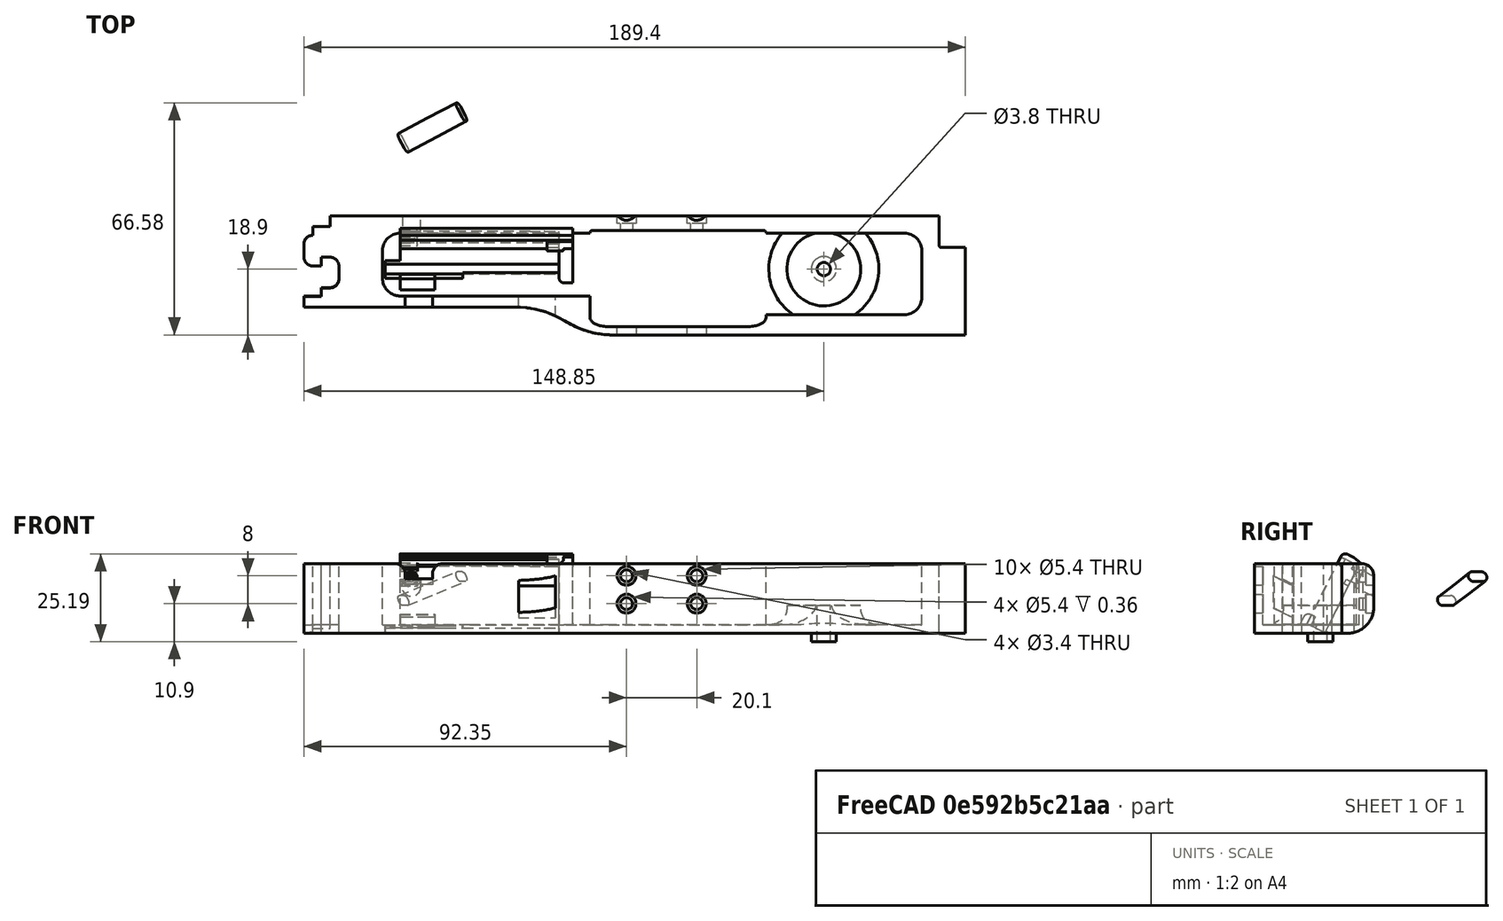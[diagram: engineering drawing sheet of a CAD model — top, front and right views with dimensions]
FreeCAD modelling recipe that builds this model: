
FCSTD DOCUMENT  (FreeCAD 0.19R0.19.2)
Label: v0_995
License: All rights reserved
LicenseURL: http://en.wikipedia.org/wiki/All_rights_reserved
objects: Sketcher::SketchObject×37, Part::Extrusion×31, Part::MultiFuse×19, Part::Box×14, Part::Cut×14, Part::Fillet×13, App::MeasureDistance×4, Part::Cylinder×4, Part::Revolution×1, Mesh::Feature×1
note: 133 computed .brp shape members not serialized (recipe doc carries the construction recipe); baked Part::Feature solids carry a one-line shape summary decoded from their .brp

FEATURE [Sketcher::SketchObject] Sketch
  FullyConstrained = true
  sketch-geometry (36):
    g0: LineSegment StartX=0 StartY=0 StartZ=0 EndX=154.4 EndY=0 EndZ=0
    g1: LineSegment StartX=154.4 StartY=0 StartZ=0 EndX=154.4 EndY=-7.6 EndZ=0
    g2: LineSegment StartX=32.5209 StartY=-26.2 StartZ=0 EndX=-7.5 EndY=-26.2 EndZ=0
    g3-g7: Circle x5 (B-spline internal-alignment scaffolding for g8; pole/knot coordinates omitted)
    g8: BSplineCurve PolesCount=5 KnotsCount=3 Degree=3 IsPeriodic=0
    g9: GeomPoint X=61.85 Y=-33.8 Z=0
    g10: GeomPoint X=47.185 Y=-29.9 Z=0
    g11: GeomPoint X=32.5209 Y=-26.2 Z=0
    g12: Circle CenterX=121.35 CenterY=-14.3 CenterZ=0 NormalX=0 NormalY=0 NormalZ=1 AngleXU=0 Radius=3.25
    g13: LineSegment StartX=-7.5 StartY=-26.2 StartZ=0 EndX=-27.5 EndY=-26.2 EndZ=0
    g14: LineSegment StartX=-20 StartY=0 StartZ=0 EndX=0 EndY=0 EndZ=0
    g15: LineSegment StartX=-25 StartY=-3.1 StartZ=0 EndX=-20 EndY=-3.1 EndZ=0
    g16: LineSegment StartX=-25 StartY=-3.1 StartZ=0 EndX=-25 EndY=-5.6 EndZ=0
    g17: LineSegment StartX=-27.5 StartY=-8.1 StartZ=0 EndX=-27.5 EndY=-11.85 EndZ=0
    g18: ArcOfCircle CenterX=-25 CenterY=-8.1 CenterZ=0 NormalX=0 NormalY=0 NormalZ=1 AngleXU=0 Radius=2.5 StartAngle=1.5708 EndAngle=3.14159
    g19: LineSegment StartX=-25 StartY=-14.35 StartZ=0 EndX=-22.5 EndY=-14.35 EndZ=0
    g20: ArcOfCircle CenterX=-25 CenterY=-11.85 CenterZ=0 NormalX=0 NormalY=0 NormalZ=1 AngleXU=0 Radius=2.5 StartAngle=3.14159 EndAngle=4.71239
    g21: LineSegment StartX=-22.5 StartY=-14.35 StartZ=0 EndX=-22.5 EndY=-11.85 EndZ=0
    g22: LineSegment StartX=-22.5 StartY=-11.85 StartZ=0 EndX=-20 EndY=-11.85 EndZ=0
    g23: ArcOfCircle CenterX=-20 CenterY=-14.35 CenterZ=0 NormalX=0 NormalY=0 NormalZ=1 AngleXU=0 Radius=2.5 StartAngle=8e-16 EndAngle=1.5708
    g24: LineSegment StartX=-17.5 StartY=-14.35 StartZ=0 EndX=-17.5 EndY=-18.1 EndZ=0
    g25: ArcOfCircle CenterX=-20 CenterY=-18.1 CenterZ=0 NormalX=0 NormalY=0 NormalZ=1 AngleXU=0 Radius=2.5 StartAngle=4.71239 EndAngle=6.28319
    g26: LineSegment StartX=-22.5 StartY=-20.6 StartZ=0 EndX=-20 EndY=-20.6 EndZ=0
    g27: LineSegment StartX=-22.5 StartY=-20.6 StartZ=0 EndX=-22.5 EndY=-23.1 EndZ=0
    g28: LineSegment StartX=-27.5 StartY=-23.1 StartZ=0 EndX=-22.5 EndY=-23.1 EndZ=0
    g29: LineSegment StartX=-20 StartY=-3.1 StartZ=0 EndX=-20 EndY=0 EndZ=0
    g30: LineSegment StartX=-27.5 StartY=-23.1 StartZ=0 EndX=-27.5 EndY=-26.2 EndZ=0
    g31: LineSegment StartX=154.4 StartY=-7.6 StartZ=0 EndX=154.4 EndY=-8.6 EndZ=0
    g32: ArcOfCircle CenterX=154.9 CenterY=-8.6 CenterZ=0 NormalX=0 NormalY=0 NormalZ=1 AngleXU=0 Radius=0.5 StartAngle=3.14159 EndAngle=4.71239
    g33: LineSegment StartX=154.9 StartY=-9.1 StartZ=0 EndX=161.9 EndY=-9.1 EndZ=0
    g34: LineSegment StartX=161.9 StartY=-9.1 StartZ=0 EndX=161.9 EndY=-33.8 EndZ=0
    g35: LineSegment StartX=161.9 StartY=-33.8 StartZ=0 EndX=61.85 EndY=-33.8 EndZ=0
  constraints (72):
    c: PointOnObject(g0,g-2)
    c: Horizontal(g0)
    c: Distance(g0) = 154.4
    c: DistanceY(g-1,g0) = 0
    c: Vertical(g1)
    c: Distance(g1) = 7.6
    c: Coincident(g1,g0)
    c: Horizontal(g2)
    c: Block(g2)
    c: Weight(g3) = 1
    c: Coincident(g8,g2)
    c: InternalAlignment(g3-g7 -> g8) x5
    c: InternalAlignment(g9,g8)
    c: InternalAlignment(g10,g8)
    c: InternalAlignment(g11,g8)
    c: Block(g12)
    c: Coincident(g13,g2)
    c: Horizontal(g13)
    c: Distance(g13) = 20
    c: Horizontal(g14)
    c: Distance(g14) = 20
    c: Coincident(g14,g0)
    c: Horizontal(g15)
    c: Vertical(g16)
    c: Coincident(g16,g15)
    c: Vertical(g17)
    c: Coincident(g18,g16)
    c: Block(g18)
    c: Coincident(g17,g18)
    c: Horizontal(g19)
    c: Coincident(g20,g17)
    c: Block(g20)
    c: Block(g19)
    c: Vertical(g21)
    c: Coincident(g21,g19)
    c: Horizontal(g22)
    c: Coincident(g22,g21)
    c: Coincident(g23,g22)
    c: Vertical(g24)
    c: Block(g23)
    c: Coincident(g24,g23)
    c: Coincident(g25,g24)
    c: Block(g25)
    c: Horizontal(g26)
    c: Coincident(g26,g25)
    c: Vertical(g27)
    c: Coincident(g27,g26)
    c: Horizontal(g28)
    c: Coincident(g28,g27)
    c: Block(g15)
    c: Block(g28)
    c: Coincident(g29,g15)
    c: Coincident(g29,g14)
    c: Vertical(g29)
    c: Coincident(g30,g28)
    c: Coincident(g30,g13)
    c: Vertical(g30)
    c: Vertical(g31)
    c: Distance(g31) = 1
    c: Coincident(g31,g1)
    c: Coincident(g32,g31)
    c: Block(g32)
    c: Coincident(g33,g32)
    c: Horizontal(g33)
    c: Coincident(g34,g33)
    c: Vertical(g34)
    c: Block(g34)
    c: Coincident(g35,g34)
    c: Horizontal(g35)
    c: Block(g35)
    c: Coincident(g8,g35)
    c: Block(g8)
FEATURE [Part::Extrusion] Extrude  label="mainBodyBaseExtrude"
  Base = -> Sketch
  Dir = (0,0,1)
  DirMode = 2
  FaceMakerClass = Part::FaceMakerBullseye
  LengthFwd = 2.4
  LengthRev = 0
  Solid = true
  Symmetric = false
FEATURE [Sketcher::SketchObject] Sketch001
  FullyConstrained = true
  sketch-geometry (75):
    g0: ArcOfCircle CenterX=144.4 CenterY=-10 CenterZ=0 NormalX=0 NormalY=0 NormalZ=1 AngleXU=0 Radius=5 StartAngle=4.345e-13 EndAngle=1.5708
    g1: LineSegment StartX=32.5209 StartY=-26.2 StartZ=0 EndX=-7.49911 EndY=-26.2 EndZ=0
    g2: LineSegment StartX=0 StartY=0 StartZ=0 EndX=154.4 EndY=0 EndZ=0
    g3-g7: Circle x5 (B-spline internal-alignment scaffolding for g8; pole/knot coordinates omitted)
    g8: BSplineCurve PolesCount=5 KnotsCount=3 Degree=3 IsPeriodic=0
    g9: GeomPoint X=61.85 Y=-33.8 Z=0
    g10: GeomPoint X=47.1857 Y=-29.9 Z=0
    g11: GeomPoint X=32.5209 Y=-26.2 Z=0
    g12: LineSegment StartX=154.4 StartY=0 StartZ=0 EndX=154.4 EndY=-7.6 EndZ=0
    g13: LineSegment StartX=20 StartY=-5 StartZ=0 EndX=54.35 EndY=-5 EndZ=0
    g14: LineSegment StartX=104.85 StartY=-5 StartZ=0 EndX=144.4 EndY=-5 EndZ=0
    g15: LineSegment StartX=54.35 StartY=-23 StartZ=0 EndX=20 EndY=-23 EndZ=0
    g16: LineSegment StartX=-27.4991 StartY=-26.2 StartZ=0 EndX=-7.49911 EndY=-26.2 EndZ=0
    g17: LineSegment StartX=-20 StartY=0 StartZ=0 EndX=0 EndY=0 EndZ=0
    g18: LineSegment StartX=-27.4991 StartY=-23.2 StartZ=0 EndX=-22.5 EndY=-23.2 EndZ=0
    g19: LineSegment StartX=-22.5 StartY=-20.7 StartZ=0 EndX=-22.5 EndY=-23.2 EndZ=0
    g20: LineSegment StartX=-22.5 StartY=-20.7 StartZ=0 EndX=-20 EndY=-20.7 EndZ=0
    g21: ArcOfCircle CenterX=-20 CenterY=-18.2 CenterZ=0 NormalX=0 NormalY=0 NormalZ=1 AngleXU=0 Radius=2.5 StartAngle=4.71239 EndAngle=6.28319
    g22: LineSegment StartX=-17.5 StartY=-14.4 StartZ=0 EndX=-17.5 EndY=-18.2 EndZ=0
    g23: ArcOfCircle CenterX=-20 CenterY=-14.4 CenterZ=0 NormalX=0 NormalY=0 NormalZ=1 AngleXU=0 Radius=2.5 StartAngle=9e-16 EndAngle=1.5708
    g24: LineSegment StartX=-22.5 StartY=-11.9 StartZ=0 EndX=-20 EndY=-11.9 EndZ=0
    g25: LineSegment StartX=-22.5 StartY=-14.4 StartZ=0 EndX=-22.5 EndY=-11.9 EndZ=0
    g26: LineSegment StartX=-25 StartY=-14.4 StartZ=0 EndX=-22.5 EndY=-14.4 EndZ=0
    g27: ArcOfCircle CenterX=-25 CenterY=-11.9 CenterZ=0 NormalX=0 NormalY=0 NormalZ=1 AngleXU=0 Radius=2.5 StartAngle=3.14159 EndAngle=4.71239
    g28: LineSegment StartX=-27.5 StartY=-8.1 StartZ=0 EndX=-27.5 EndY=-11.9 EndZ=0
    g29: ArcOfCircle CenterX=-25 CenterY=-8.1 CenterZ=0 NormalX=0 NormalY=0 NormalZ=1 AngleXU=0 Radius=2.5 StartAngle=1.5708 EndAngle=3.14159
    g30: LineSegment StartX=-25 StartY=-3.1 StartZ=0 EndX=-25 EndY=-5.6 EndZ=0
    g31: LineSegment StartX=-20 StartY=-3.1 StartZ=0 EndX=-25 EndY=-3.1 EndZ=0
    g32: LineSegment StartX=-20 StartY=0 StartZ=0 EndX=-20 EndY=-3.1 EndZ=0
    g33: LineSegment StartX=-27.4991 StartY=-26.2 StartZ=0 EndX=-27.4991 EndY=-23.2 EndZ=0
    g34: LineSegment StartX=4.09e-14 StartY=-5 StartZ=0 EndX=20 EndY=-5 EndZ=0
    g35: ArcOfCircle CenterX=7.1e-15 CenterY=-18 CenterZ=0 NormalX=0 NormalY=0 NormalZ=1 AngleXU=0 Radius=5 StartAngle=3.14159 EndAngle=4.71239
    g36: ArcOfCircle CenterX=4.26e-14 CenterY=-10 CenterZ=0 NormalX=0 NormalY=0 NormalZ=1 AngleXU=0 Radius=5 StartAngle=1.5708 EndAngle=3.14159
    g37: LineSegment StartX=-5 StartY=-18 StartZ=0 EndX=-5 EndY=-10 EndZ=0
    g38: LineSegment StartX=6.2e-15 StartY=-23 StartZ=0 EndX=20 EndY=-23 EndZ=0
    g39: LineSegment StartX=154.4 StartY=-7.6 StartZ=0 EndX=154.4 EndY=-8.6 EndZ=0
    g40: LineSegment StartX=154.9 StartY=-9.1 StartZ=0 EndX=161.9 EndY=-9.1 EndZ=0
    g41: ArcOfCircle CenterX=154.9 CenterY=-8.6 CenterZ=0 NormalX=0 NormalY=0 NormalZ=1 AngleXU=0 Radius=0.5 StartAngle=3.14159 EndAngle=4.71299
    g42: LineSegment StartX=104.85 StartY=-28.3916 StartZ=0 EndX=144.408 EndY=-28.3916 EndZ=0
    g43: LineSegment StartX=149.4 StartY=-10 StartZ=0 EndX=149.4 EndY=-23.4 EndZ=0
    g44: ArcOfCircle CenterX=144.408 CenterY=-23.4 CenterZ=0 NormalX=0 NormalY=0 NormalZ=1 AngleXU=0 Radius=4.99164 StartAngle=4.71239 EndAngle=6.28319
    g45: LineSegment StartX=104.85 StartY=-28.3916 StartZ=0 EndX=104.85 EndY=-28.7833 EndZ=0
    g46: LineSegment StartX=54.35 StartY=-28.7916 StartZ=0 EndX=54.35 EndY=-23 EndZ=0
    g47: LineSegment StartX=161.9 StartY=-33.8 StartZ=0 EndX=161.9 EndY=-9.1 EndZ=0
    g48: LineSegment StartX=61.85 StartY=-33.8 StartZ=0 EndX=161.9 EndY=-33.8 EndZ=0
    g49: Circle CenterX=54.35 CenterY=-28.7916 CenterZ=0 NormalX=0 NormalY=0 NormalZ=1 AngleXU=0 Radius=1
    g50: Circle CenterX=54.35 CenterY=-31.7916 CenterZ=0 NormalX=0 NormalY=0 NormalZ=1 AngleXU=0 Radius=1
    g51: Circle CenterX=57.35 CenterY=-31.7916 CenterZ=0 NormalX=0 NormalY=0 NormalZ=1 AngleXU=0 Radius=1
    g52: BSplineCurve PolesCount=3 KnotsCount=2 Degree=2 IsPeriodic=0
    g53: GeomPoint X=54.35 Y=-28.7916 Z=0
    g54: GeomPoint X=57.35 Y=-31.7916 Z=0
    g55: Circle CenterX=104.85 CenterY=-28.7833 CenterZ=0 NormalX=0 NormalY=0 NormalZ=1 AngleXU=0 Radius=1
    g56: Circle CenterX=104.85 CenterY=-31.7916 CenterZ=0 NormalX=0 NormalY=0 NormalZ=1 AngleXU=0 Radius=1
    g57: Circle CenterX=101.85 CenterY=-31.7916 CenterZ=0 NormalX=0 NormalY=0 NormalZ=1 AngleXU=0 Radius=1
    g58: BSplineCurve PolesCount=3 KnotsCount=2 Degree=2 IsPeriodic=0
    g59: GeomPoint X=104.85 Y=-28.7833 Z=0
    g60: GeomPoint X=101.85 Y=-31.7916 Z=0
    g61: LineSegment StartX=57.35 StartY=-31.7916 StartZ=0 EndX=101.85 EndY=-31.7916 EndZ=0
    g62: Circle CenterX=54.35 CenterY=-5 CenterZ=0 NormalX=0 NormalY=0 NormalZ=1 AngleXU=0 Radius=1
    g63: Circle CenterX=54.35 CenterY=-4 CenterZ=0 NormalX=0 NormalY=0 NormalZ=1 AngleXU=0 Radius=1
    g64: Circle CenterX=55.15 CenterY=-4 CenterZ=0 NormalX=0 NormalY=0 NormalZ=1 AngleXU=0 Radius=1
    g65: BSplineCurve PolesCount=3 KnotsCount=2 Degree=2 IsPeriodic=0
    g66: GeomPoint X=54.35 Y=-5 Z=0
    g67: GeomPoint X=55.15 Y=-4 Z=0
    g68: Circle CenterX=104.85 CenterY=-5 CenterZ=0 NormalX=0 NormalY=0 NormalZ=1 AngleXU=0 Radius=1
    g69: Circle CenterX=104.85 CenterY=-4 CenterZ=0 NormalX=0 NormalY=0 NormalZ=1 AngleXU=0 Radius=1
    g70: Circle CenterX=104.05 CenterY=-4 CenterZ=0 NormalX=0 NormalY=0 NormalZ=1 AngleXU=0 Radius=1
    g71: BSplineCurve PolesCount=3 KnotsCount=2 Degree=2 IsPeriodic=0
    g72: GeomPoint X=104.85 Y=-5 Z=0
    g73: GeomPoint X=104.05 Y=-4 Z=0
    g74: LineSegment StartX=104.05 StartY=-4 StartZ=0 EndX=55.15 EndY=-4 EndZ=0
  constraints (156):
    c: PointOnObject(g2,g-2)
    c: DistanceY(g-1,g2) = 0
    c: Block(g0)
    c: Horizontal(g1)
    c: Distance(g1) = 40.02
    c: Horizontal(g2)
    c: Block(g2)
    c: Weight(g3) = 1
    c: Equal(g3, g4-g7) x4
    c: Coincident(g8,g1)
    c: InternalAlignment(g3-g7 -> g8) x5
    c: InternalAlignment(g9,g8)
    c: InternalAlignment(g10,g8)
    c: InternalAlignment(g11,g8)
    c: Vertical(g12)
    c: Coincident(g12,g2)
    c: Distance(g12) = 7.6
    c: Block(g12)
    c: Horizontal(g13)
    c: Coincident(g14,g0)
    c: Horizontal(g14)
    c: Horizontal(g15)
    c: Horizontal(g16)
    c: Distance(g16) = 20
    c: Coincident(g1,g16)
    c: Horizontal(g17)
    c: Distance(g17) = 20
    c: Coincident(g17,g2)
    c: Horizontal(g31)
    c: Vertical(g30)
    c: Coincident(g29,g30)
    c: Vertical(g28)
    c: Block(g29)
    c: Coincident(g27,g28)
    c: Block(g27)
    c: Horizontal(g26)
    c: Coincident(g26,g27)
    c: Vertical(g25)
    c: Coincident(g25,g26)
    c: Horizontal(g24)
    c: Coincident(g23,g24)
    c: Block(g23)
    c: Vertical(g22)
    c: Coincident(g21,g22)
    c: Block(g21)
    c: Horizontal(g20)
    c: Coincident(g20,g21)
    c: Vertical(g19)
    c: Coincident(g19,g20)
    c: Horizontal(g18)
    c: Coincident(g18,g19)
    c: Coincident(g32,g17)
    c: Coincident(g32,g31)
    c: Vertical(g32)
    c: Coincident(g33,g16)
    c: Coincident(g33,g18)
    c: Vertical(g33)
    c: Block(g33)
    c: Block(g18)
    c: Block(g22)
    c: Block(g26)
    c: Block(g25)
    c: Block(g24)
    c: Block(g28)
    c: Block(g31)
    c: Block(g30)
    c: Horizontal(g34)
    c: Distance(g34) = 20
    c: Block(g35)
    c: Block(g36)
    c: Coincident(g37,g35)
    c: Coincident(g37,g36)
    c: Vertical(g37)
    c: Coincident(g38,g35)
    c: Coincident(g38,g15)
    c: Horizontal(g38)
    c: Block(g38)
    c: Block(g34)
    c: Block(g13)
    c: Vertical(g39)
    c: Distance(g39) = 1
    c: Coincident(g39,g12)
    c: Horizontal(g40)
    c: Coincident(g41,g39)
    c: Coincident(g41,g40)
    c: Block(g39)
    c: Block(g41)
    c: Horizontal(g42)
    c: Vertical(g43)
    c: Distance(g43) = 13.4
    c: Coincident(g43,g0)
    c: Block(g42)
    c: Block(g43)
    c: Coincident(g44,g43)
    c: Coincident(g44,g42)
    c: Block(g44)
    c: Distance(g15) = 34.35
    c: Coincident(g45,g42)
    c: Vertical(g45)
    c: Coincident(g46,g15)
    c: Vertical(g46)
    c: Coincident(g47,g40)
    c: Vertical(g47)
    c: Block(g47)
    c: Coincident(g48,g47)
    c: Horizontal(g48)
    c: Block(g48)
    c: Coincident(g8,g48)
    c: Block(g8)
    c: Coincident(g52,g46)
    c: Weight(g49) = 1
    c: Equal(g49,g50)
    c: Equal(g49,g51)
    c: InternalAlignment(g49,g52)
    c: InternalAlignment(g50,g52)
    c: InternalAlignment(g51,g52)
    c: InternalAlignment(g53,g52)
    c: InternalAlignment(g54,g52)
    c: Coincident(g58,g45)
    c: Weight(g55) = 1
    c: Equal(g55,g56)
    c: Equal(g55,g57)
    c: InternalAlignment(g55,g58)
    c: InternalAlignment(g56,g58)
    c: InternalAlignment(g57,g58)
    c: InternalAlignment(g59,g58)
    c: InternalAlignment(g60,g58)
    c: Block(g58)
    c: Block(g52)
    c: Coincident(g61,g52)
    c: Coincident(g61,g58)
    c: Horizontal(g61)
    c: Block(g14)
    c: Coincident(g65,g13)
    c: Weight(g62) = 1
    c: Equal(g62,g63)
    c: Equal(g62,g64)
    c: InternalAlignment(g62,g65)
    c: InternalAlignment(g63,g65)
    c: InternalAlignment(g64,g65)
    c: InternalAlignment(g66,g65)
    c: InternalAlignment(g67,g65)
    c: Block(g65)
    c: Coincident(g71,g14)
    c: Weight(g68) = 1
    c: Equal(g68,g69)
    c: Equal(g68,g70)
    c: InternalAlignment(g68,g71)
    c: InternalAlignment(g69,g71)
    c: InternalAlignment(g70,g71)
    c: InternalAlignment(g72,g71)
    c: InternalAlignment(g73,g71)
    c: Block(g71)
    c: Coincident(g74,g71)
    c: Coincident(g74,g65)
    c: Horizontal(g74)
FEATURE [Sketcher::SketchObject] Sketch005
  FullyConstrained = true
  Placement = pos=(0,0,0) rot=(1,0,0;1.5708rad)
  sketch-geometry (4):
    g0: Circle CenterX=84.95 CenterY=16.5 CenterZ=0 NormalX=0 NormalY=0 NormalZ=1 AngleXU=0 Radius=1.7
    g1: Circle CenterX=84.95 CenterY=8.5 CenterZ=0 NormalX=0 NormalY=0 NormalZ=1 AngleXU=0 Radius=1.7
    g2: Circle CenterX=64.85 CenterY=8.5 CenterZ=0 NormalX=0 NormalY=0 NormalZ=1 AngleXU=0 Radius=1.7
    g3: Circle CenterX=64.85 CenterY=16.5 CenterZ=0 NormalX=0 NormalY=0 NormalZ=1 AngleXU=0 Radius=1.7
  constraints (4):
    c: Block(g0)
    c: Block(g1)
    c: Block(g2)
    c: Block(g3)
FEATURE [Part::Extrusion] Extrude004  label="removeFromMainBodyToCreateScrewHolesForSolenoidExtrude004"
  Base = -> Sketch005
  Dir = (0,-1,1.1e-15)
  DirMode = 2
  FaceMakerClass = Part::FaceMakerBullseye
  LengthFwd = 10
  LengthRev = 0
  Solid = true
  Symmetric = false
FEATURE [Sketcher::SketchObject] Sketch004
  FullyConstrained = true
  Placement = pos=(0,0,0) rot=(1,0,0;1.5708rad)
  sketch-geometry (12):
    g0: LineSegment StartX=15.75 StartY=2.5 StartZ=0 EndX=15.75 EndY=0 EndZ=0
    g1: Circle CenterX=15.75 CenterY=2.5 CenterZ=0 NormalX=0 NormalY=0 NormalZ=1 AngleXU=0 Radius=1
    g2: Circle CenterX=10.55 CenterY=2.5 CenterZ=0 NormalX=0 NormalY=0 NormalZ=1 AngleXU=0 Radius=1
    g3: Circle CenterX=10.55 CenterY=8 CenterZ=0 NormalX=0 NormalY=0 NormalZ=1 AngleXU=0 Radius=1
    g4: BSplineCurve PolesCount=3 KnotsCount=2 Degree=2 IsPeriodic=0
    g5: GeomPoint X=15.75 Y=2.5 Z=0
    g6: GeomPoint X=10.55 Y=8 Z=0
    g7: LineSegment StartX=1.9 StartY=8 StartZ=0 EndX=10.55 EndY=8 EndZ=0
    g8: LineSegment StartX=1.9 StartY=-2.4 StartZ=0 EndX=1.9 EndY=8 EndZ=0
    g9: LineSegment StartX=3.30092 StartY=-2.4 StartZ=0 EndX=3.30092 EndY=0 EndZ=0
    g10: LineSegment StartX=15.75 StartY=0 StartZ=0 EndX=3.30092 EndY=0 EndZ=0
    g11: LineSegment StartX=3.30092 StartY=-2.4 StartZ=0 EndX=1.9 EndY=-2.4 EndZ=0
  constraints (26):
    c: Vertical(g0)
    c: Distance(g0) = 2.5
    c: Coincident(g4,g0)
    c: Weight(g1) = 1
    c: Equal(g1,g2)
    c: Equal(g1,g3)
    c: InternalAlignment(g1,g4)
    c: InternalAlignment(g2,g4)
    c: InternalAlignment(g3,g4)
    c: InternalAlignment(g5,g4)
    c: InternalAlignment(g6,g4)
    c: Block(g4)
    c: Coincident(g7,g4)
    c: Horizontal(g7)
    c: Vertical(g8)
    c: Coincident(g8,g7)
    c: Block(g8)
    c: Vertical(g9)
    c: Coincident(g10,g0)
    c: PointOnObject(g10,g-1)
    c: Horizontal(g10)
    c: Coincident(g10,g9)
    c: Block(g9)
    c: Coincident(g11,g9)
    c: Coincident(g11,g8)
    c: Horizontal(g11)
FEATURE [Sketcher::SketchObject] Sketch007
  FullyConstrained = true
  Placement = pos=(0,-14.3,2.37) rot=(-1,0,0;2.03453rad)
  sketch-geometry (6):
    g0: LineSegment StartX=0 StartY=0 StartZ=0 EndX=45.5 EndY=0 EndZ=0
    g1: LineSegment StartX=0 StartY=0 StartZ=0 EndX=0 EndY=-21.2 EndZ=0
    g2: LineSegment StartX=45.5 StartY=0 StartZ=0 EndX=49.5 EndY=0 EndZ=0
    g3: LineSegment StartX=49.5 StartY=0 StartZ=0 EndX=49.5 EndY=-21.2 EndZ=0
    g4: LineSegment StartX=49.5 StartY=-21.2 StartZ=0 EndX=0 EndY=-21.2 EndZ=0
    g5: Circle CenterX=3.25 CenterY=-18.05 CenterZ=0 NormalX=0 NormalY=0 NormalZ=1 AngleXU=0 Radius=1.6
  constraints (15):
    c: Coincident(g0,g-1)
    c: Horizontal(g0)
    c: Distance(g0) = 45.5
    c: Coincident(g1,g0)
    c: Vertical(g1)
    c: Horizontal(g2)
    c: Distance(g2) = 4
    c: Coincident(g2,g0)
    c: Coincident(g3,g2)
    c: Vertical(g3)
    c: Block(g3)
    c: Coincident(g4,g3)
    c: Horizontal(g4)
    c: Coincident(g4,g1)
    c: Block(g5)
FEATURE [Part::Extrusion] Extrude005  label="solenoidDriverHolderExtrude005"
  Base = -> Sketch007
  Dir = (0,0.894389,-0.447291)
  DirMode = 2
  FaceMakerClass = Part::FaceMakerBullseye
  LengthFwd = 10
  LengthRev = 0
  Placement = pos=(0,0,-2) rot=(0,0,1;0rad)
  Solid = true
  Symmetric = false
FEATURE [Sketcher::SketchObject] Sketch008
  FullyConstrained = false
  Placement = pos=(0,-4.3,-2.6) rot=(-1,0,0;2.03453rad)
  sketch-geometry (1):
    g0: Circle CenterX=42.25 CenterY=-3.15 CenterZ=0 NormalX=0 NormalY=0 NormalZ=1 AngleXU=0 Radius=4.5
FEATURE [Sketcher::SketchObject] Sketch009
  FullyConstrained = true
  Placement = pos=(0,-4.3,-2.6) rot=(-1,0,0;2.03453rad)
  sketch-geometry (1):
    g0: Circle CenterX=3.25 CenterY=-18.0217 CenterZ=0 NormalX=0 NormalY=0 NormalZ=1 AngleXU=0 Radius=2.8
  constraints (1):
    c: Block(g0)
FEATURE [Sketcher::SketchObject] Sketch010
  FullyConstrained = true
  Placement = pos=(0,-14.3,2.37) rot=(-1,0,0;2.03453rad)
  sketch-geometry (1):
    g0: Circle CenterX=3.25 CenterY=-18.05 CenterZ=0 NormalX=0 NormalY=0 NormalZ=1 AngleXU=0 Radius=1.6
  constraints (1):
    c: Block(g0)
FEATURE [Part::Extrusion] Extrude008  label="removeFromScrewHole3"
  Base = -> Sketch010
  Dir = (0,0.894389,-0.447291)
  DirMode = 2
  FaceMakerClass = Part::FaceMakerBullseye
  LengthFwd = -25
  LengthRev = 0
  Placement = pos=(0,4,-4) rot=(0,0,1;0rad)
  Solid = true
  Symmetric = false
FEATURE [Sketcher::SketchObject] Sketch011
  FullyConstrained = true
  Placement = pos=(0,-14.3,2.37) rot=(-1,0,0;2.03453rad)
  sketch-geometry (4):
    g0: LineSegment StartX=49.5 StartY=-21.2 StartZ=0 EndX=49.5 EndY=-22.8 EndZ=0
    g1: LineSegment StartX=49.5 StartY=-22.8 StartZ=0 EndX=0.002238 EndY=-22.8 EndZ=0
    g2: LineSegment StartX=0.002238 StartY=-21.2 StartZ=0 EndX=0.002238 EndY=-22.8 EndZ=0
    g3: LineSegment StartX=49.5 StartY=-21.2 StartZ=0 EndX=0.002238 EndY=-21.2 EndZ=0
  constraints (10):
    c: Vertical(g0)
    c: Distance(g0) = 1.6
    c: Coincident(g1,g0)
    c: Horizontal(g1)
    c: Vertical(g2)
    c: Coincident(g2,g1)
    c: Coincident(g3,g0)
    c: Coincident(g3,g2)
    c: Horizontal(g3)
    c: Block(g3)
FEATURE [Part::Extrusion] Extrude009  label="solenoidDriverTopLipFront"
  Base = -> Sketch011
  Dir = (0,0.894389,-0.447291)
  DirMode = 2
  FaceMakerClass = Part::FaceMakerBullseye
  LengthFwd = -2
  LengthRev = 0
  Placement = pos=(0,-2.9,-0.35) rot=(0,0,1;0rad)
  Solid = true
  Symmetric = false
FEATURE [Sketcher::SketchObject] Sketch012
  FullyConstrained = true
  Placement = pos=(0,-14.3,2.37) rot=(-1,0,0;2.03453rad)
  sketch-geometry (4):
    g0: LineSegment StartX=49.5 StartY=-21.2 StartZ=0 EndX=49.5 EndY=-22.8 EndZ=0
    g1: LineSegment StartX=49.5 StartY=-22.8 StartZ=0 EndX=0.002238 EndY=-22.8 EndZ=0
    g2: LineSegment StartX=0.002238 StartY=-21.2 StartZ=0 EndX=0.002238 EndY=-22.8 EndZ=0
    g3: LineSegment StartX=49.5 StartY=-21.2 StartZ=0 EndX=0.002238 EndY=-21.2 EndZ=0
  constraints (10):
    c: Vertical(g0)
    c: Distance(g0) = 1.6
    c: Coincident(g1,g0)
    c: Horizontal(g1)
    c: Vertical(g2)
    c: Coincident(g2,g1)
    c: Coincident(g3,g0)
    c: Coincident(g3,g2)
    c: Horizontal(g3)
    c: Block(g3)
FEATURE [Part::Extrusion] Extrude010  label="solenoidDriverTopLipLowerExtrude010"
  Base = -> Sketch012
  Dir = (0,0.894389,-0.447291)
  DirMode = 2
  FaceMakerClass = Part::FaceMakerBullseye
  LengthFwd = 5.05
  LengthRev = 0
  Solid = true
  Symmetric = false
FEATURE [Sketcher::SketchObject] Sketch015
  FullyConstrained = true
  Placement = pos=(0,-14.3,2.37) rot=(-1,0,0;2.03453rad)
  sketch-geometry (4):
    g0: LineSegment StartX=0 StartY=1.5 StartZ=0 EndX=0 EndY=0 EndZ=0
    g1: LineSegment StartX=0 StartY=1.5 StartZ=0 EndX=5 EndY=1.5 EndZ=0
    g2: LineSegment StartX=5 StartY=1.5 StartZ=0 EndX=5 EndY=0 EndZ=0
    g3: LineSegment StartX=0 StartY=0 StartZ=0 EndX=5 EndY=0 EndZ=0
  constraints (13):
    c: Vertical(g0)
    c: Distance(g0) = 1.5
    c: Horizontal(g1)
    c: Distance(g1) = 5
    c: Coincident(g1,g0)
    c: Vertical(g2)
    c: Distance(g2) = 1.5
    c: Coincident(g2,g1)
    c: Block(g1)
    c: Block(g2)
    c: Block(g0)
    c: Coincident(g3,g0)
    c: Coincident(g3,g2)
FEATURE [Part::Extrusion] Extrude013  label="solenoidDriverBottomLipTopExtrude012"
  Base = -> Sketch015
  Dir = (0,0.894389,-0.447291)
  DirMode = 2
  FaceMakerClass = Part::FaceMakerBullseye
  LengthFwd = -6.5
  LengthRev = 0
  Placement = pos=(0,-14.15,19.65) rot=(1,0,0;1.5708rad)
  Solid = true
  Symmetric = false
FEATURE [Sketcher::SketchObject] Sketch016
  FullyConstrained = true
  Placement = pos=(0,0,0) rot=(1,0,0;1.5708rad)
  sketch-geometry (4):
    g0: Circle CenterX=84.15 CenterY=16.5 CenterZ=0 NormalX=0 NormalY=0 NormalZ=1 AngleXU=0 Radius=2.7
    g1: Circle CenterX=64.05 CenterY=16.5 CenterZ=0 NormalX=0 NormalY=0 NormalZ=1 AngleXU=0 Radius=2.7
    g2: Circle CenterX=64.05 CenterY=8.5 CenterZ=0 NormalX=0 NormalY=0 NormalZ=1 AngleXU=0 Radius=2.7
    g3: Circle CenterX=84.15 CenterY=8.5 CenterZ=0 NormalX=0 NormalY=0 NormalZ=1 AngleXU=0 Radius=2.7
  constraints (4):
    c: Block(g0)
    c: Block(g1)
    c: Block(g3)
    c: Block(g2)
FEATURE [Part::Extrusion] Extrude014  label="removeFromMainBodyToCreateScrewHoleCounterSinks"
  Base = -> Sketch016
  Dir = (0,-1,1.1e-15)
  DirMode = 2
  FaceMakerClass = Part::FaceMakerBullseye
  LengthFwd = 1.9
  LengthRev = 0
  Placement = pos=(0.8,-0.36,0) rot=(0,0,1;0rad)
  Solid = true
  Symmetric = false
FEATURE [Part::Extrusion] Extrude015  label="removeFromScrewHole2Extrude007"
  Base = -> Sketch009
  Dir = (0,0.894389,-0.447291)
  DirMode = 2
  FaceMakerClass = Part::FaceMakerBullseye
  LengthFwd = 10
  LengthRev = 0
  Placement = pos=(0,-8,2) rot=(0,0,1;0rad)
  Solid = true
  Symmetric = false
FEATURE [Sketcher::SketchObject] Sketch017
  FullyConstrained = true
  Placement = pos=(0,-14.3,2.37) rot=(-1,0,0;2.03453rad)
  sketch-geometry (4):
    g0: LineSegment StartX=0 StartY=1.5 StartZ=0 EndX=0 EndY=0 EndZ=0
    g1: LineSegment StartX=0 StartY=1.5 StartZ=0 EndX=5 EndY=1.5 EndZ=0
    g2: LineSegment StartX=5 StartY=1.5 StartZ=0 EndX=5 EndY=0 EndZ=0
    g3: LineSegment StartX=0 StartY=0 StartZ=0 EndX=5 EndY=0 EndZ=0
  constraints (13):
    c: Vertical(g0)
    c: Distance(g0) = 1.5
    c: Horizontal(g1)
    c: Distance(g1) = 5
    c: Coincident(g1,g0)
    c: Vertical(g2)
    c: Distance(g2) = 1.5
    c: Coincident(g2,g1)
    c: Block(g1)
    c: Block(g2)
    c: Block(g0)
    c: Coincident(g3,g0)
    c: Coincident(g3,g2)
FEATURE [Part::Extrusion] Extrude016  label="solenoidDriverBottomLipTopExtrude013"
  Base = -> Sketch017
  Dir = (0,0.894389,-0.447291)
  DirMode = 2
  FaceMakerClass = Part::FaceMakerBullseye
  LengthFwd = -6.5
  LengthRev = 0
  Placement = pos=(0,-15.45,20.3) rot=(1,0,0;1.5708rad)
  Solid = true
  Symmetric = false
FEATURE [Part::Fillet] Fillet005  label="solenoidDriverBottomLipTopFillet005"
  Base = -> Extrude016
  Edges = 1 edges r=1.4: [Edge6]
FEATURE [Sketcher::SketchObject] Sketch018
  FullyConstrained = true
  Placement = pos=(38.5,-14.3,2.37) rot=(-1,0,0;2.03453rad)
  sketch-geometry (4):
    g0: LineSegment StartX=11 StartY=0 StartZ=0 EndX=11 EndY=1.5 EndZ=0
    g1: LineSegment StartX=11 StartY=0 StartZ=0 EndX=3.6 EndY=0 EndZ=0
    g2: LineSegment StartX=3.6 StartY=0 StartZ=0 EndX=3.6 EndY=1.5 EndZ=0
    g3: LineSegment StartX=11 StartY=1.5 StartZ=0 EndX=3.6 EndY=1.5 EndZ=0
  constraints (12):
    c: PointOnObject(g0,g-1)
    c: Vertical(g0)
    c: Distance(g0) = 1.5
    c: Horizontal(g1)
    c: Distance(g1) = 7.4
    c: Coincident(g1,g0)
    c: Block(g0)
    c: Coincident(g2,g1)
    c: Vertical(g2)
    c: Coincident(g3,g0)
    c: Horizontal(g3)
    c: Coincident(g2,g3)
FEATURE [Part::Extrusion] Extrude017
  Base = -> Sketch018
  Dir = (0,0.894389,-0.447291)
  DirMode = 2
  FaceMakerClass = Part::FaceMakerBullseye
  LengthFwd = 4
  LengthRev = 0
  Placement = pos=(0,-8.212,34.025) rot=(1,0,0;1.5708rad)
  Solid = true
  Symmetric = false
FEATURE [Sketcher::SketchObject] Sketch019
  FullyConstrained = true
  Placement = pos=(0,0,0) rot=(1,0,0;1.5708rad)
  sketch-geometry (4):
    g0: Circle CenterX=84.95 CenterY=8.5 CenterZ=0 NormalX=0 NormalY=0 NormalZ=1 AngleXU=0 Radius=2.7
    g1: Circle CenterX=64.85 CenterY=8.5 CenterZ=0 NormalX=0 NormalY=0 NormalZ=1 AngleXU=0 Radius=2.7
    g2: Circle CenterX=64.85 CenterY=16.5 CenterZ=0 NormalX=0 NormalY=0 NormalZ=1 AngleXU=0 Radius=2.7
    g3: Circle CenterX=84.95 CenterY=16.5 CenterZ=0 NormalX=0 NormalY=0 NormalZ=1 AngleXU=0 Radius=2.7
  constraints (4):
    c: Block(g3)
    c: Block(g2)
    c: Block(g0)
    c: Block(g1)
FEATURE [Part::Extrusion] Extrude019  label="removeSolenoidAdjusterHoles"
  Base = -> Sketch019
  Dir = (0,-1,1.1e-15)
  DirMode = 2
  FaceMakerClass = Part::FaceMakerBullseye
  LengthFwd = 6
  LengthRev = 0
  Placement = pos=(0,-30,0) rot=(0,0,1;0rad)
  Solid = true
  Symmetric = false
FEATURE [Sketcher::SketchObject] Sketch020
  FullyConstrained = true
  Placement = pos=(0,-14.3,2.37) rot=(-1,0,0;2.03453rad)
  sketch-geometry (6):
    g0: LineSegment StartX=45.5 StartY=-21.2 StartZ=0 EndX=49.5 EndY=-21.2 EndZ=0
    g1: LineSegment StartX=45.5 StartY=0 StartZ=0 EndX=49.5 EndY=0 EndZ=0
    g2: LineSegment StartX=49.5 StartY=0 StartZ=0 EndX=49.5 EndY=-21.2 EndZ=0
    g3: LineSegment StartX=4 StartY=0 StartZ=0 EndX=4 EndY=-21.2 EndZ=0
    g4: LineSegment StartX=45.5 StartY=-21.2 StartZ=0 EndX=4 EndY=-21.2 EndZ=0
    g5: LineSegment StartX=4 StartY=0 StartZ=0 EndX=45.5 EndY=0 EndZ=0
  constraints (16):
    c: Horizontal(g0)
    c: Distance(g0) = 4
    c: Horizontal(g1)
    c: Distance(g1) = 4
    c: Coincident(g2,g1)
    c: Coincident(g2,g0)
    c: Vertical(g2)
    c: Block(g2)
    c: Vertical(g3)
    c: Coincident(g4,g0)
    c: Horizontal(g4)
    c: Coincident(g4,g3)
    c: Coincident(g5,g1)
    c: Horizontal(g5)
    c: Block(g3)
    c: Block(g5)
FEATURE [Part::Box] Box  label="Cube"
  AttacherType = Attacher::AttachEngine3D
  Height = 10
  Length = 190
  Placement = pos=(-30,0,0) rot=(0,0,1;0rad)
  Width = 10
FEATURE [Part::Fillet] Fillet008
  Base = -> Box
  Edges = 1 edges r=7.5: [Edge11]
FEATURE [Part::Box] Box001  label="Cube001"
  AttacherType = Attacher::AttachEngine3D
  Height = 10
  Length = 190
  Placement = pos=(-35,0,0) rot=(0,0,1;0rad)
  Width = 10
FEATURE [Part::Cut] Cut  label="filletMain"
  Base = -> Box001
  Placement = pos=(0,-10,0) rot=(0,0,1;0rad)
  Tool = -> Fillet008
FEATURE [Part::Box] Box002  label="Cube002"
  AttacherType = Attacher::AttachEngine3D
  Height = 30
  Length = 190
  Placement = pos=(-20,0,0) rot=(0,0,1;0rad)
  Width = 10
FEATURE [Part::Box] Box003  label="Cube003"
  AttacherType = Attacher::AttachEngine3D
  Height = 10
  Length = 190
  Placement = pos=(-90,-50,-10) rot=(0,0,1;0rad)
  Width = 50
FEATURE [Sketcher::SketchObject] Sketch021
  FullyConstrained = true
  Placement = pos=(0,-14.3,2.37) rot=(-1,0,0;2.03453rad)
  sketch-geometry (6):
    g0: LineSegment StartX=41.65 StartY=-3.15 StartZ=0 EndX=38.95 EndY=-3.15 EndZ=0
    g1: LineSegment StartX=36.25 StartY=-3.15 StartZ=0 EndX=38.95 EndY=-3.15 EndZ=0
    g2: LineSegment StartX=41.65 StartY=-3.15 StartZ=0 EndX=41.65 EndY=-7.15 EndZ=0
    g3: LineSegment StartX=38.95 StartY=-7.15 StartZ=0 EndX=41.65 EndY=-7.15 EndZ=0
    g4: LineSegment StartX=38.95 StartY=-7.15 StartZ=0 EndX=36.25 EndY=-7.15 EndZ=0
    g5: LineSegment StartX=36.25 StartY=-3.15 StartZ=0 EndX=36.25 EndY=-7.15 EndZ=0
  constraints (16):
    c: Horizontal(g0)
    c: Distance(g0) = 2.7
    c: Horizontal(g1)
    c: Distance(g1) = 2.7
    c: Coincident(g1,g0)
    c: Block(g0)
    c: Coincident(g2,g0)
    c: Vertical(g2)
    c: Horizontal(g3)
    c: Coincident(g3,g2)
    c: Horizontal(g4)
    c: Coincident(g5,g1)
    c: Vertical(g5)
    c: Coincident(g5,g4)
    c: Block(g3)
    c: Block(g4)
FEATURE [Sketcher::SketchObject] Sketch022
  FullyConstrained = true
  Placement = pos=(0,-14.3,2.37) rot=(-1,0,0;2.03453rad)
  sketch-geometry (6):
    g0: LineSegment StartX=41.65 StartY=-3.15 StartZ=0 EndX=38.95 EndY=-3.15 EndZ=0
    g1: LineSegment StartX=36.25 StartY=-3.15 StartZ=0 EndX=38.95 EndY=-3.15 EndZ=0
    g2: LineSegment StartX=41.65 StartY=-3.15 StartZ=0 EndX=41.65 EndY=-7.15 EndZ=0
    g3: LineSegment StartX=38.95 StartY=-7.15 StartZ=0 EndX=41.65 EndY=-7.15 EndZ=0
    g4: LineSegment StartX=38.95 StartY=-7.15 StartZ=0 EndX=36.25 EndY=-7.15 EndZ=0
    g5: LineSegment StartX=36.25 StartY=-3.15 StartZ=0 EndX=36.25 EndY=-7.15 EndZ=0
  constraints (16):
    c: Horizontal(g0)
    c: Distance(g0) = 2.7
    c: Horizontal(g1)
    c: Distance(g1) = 2.7
    c: Coincident(g1,g0)
    c: Block(g0)
    c: Coincident(g2,g0)
    c: Vertical(g2)
    c: Horizontal(g3)
    c: Coincident(g3,g2)
    c: Horizontal(g4)
    c: Coincident(g5,g1)
    c: Vertical(g5)
    c: Coincident(g5,g4)
    c: Block(g3)
    c: Block(g4)
FEATURE [Sketcher::SketchObject] Sketch024
  FullyConstrained = true
  Placement = pos=(0,-14.3,2.37) rot=(-1,0,0;2.03453rad)
  sketch-geometry (4):
    g0: LineSegment StartX=49.5 StartY=-21.2 StartZ=0 EndX=49.5 EndY=-22.8 EndZ=0
    g1: LineSegment StartX=49.5 StartY=-22.8 StartZ=0 EndX=0.002238 EndY=-22.8 EndZ=0
    g2: LineSegment StartX=0.002238 StartY=-21.2 StartZ=0 EndX=0.002238 EndY=-22.8 EndZ=0
    g3: LineSegment StartX=49.5 StartY=-21.2 StartZ=0 EndX=0.002238 EndY=-21.2 EndZ=0
  constraints (10):
    c: Vertical(g0)
    c: Distance(g0) = 1.6
    c: Coincident(g1,g0)
    c: Horizontal(g1)
    c: Vertical(g2)
    c: Coincident(g2,g1)
    c: Coincident(g3,g0)
    c: Coincident(g3,g2)
    c: Horizontal(g3)
    c: Block(g3)
FEATURE [Sketcher::SketchObject] Sketch025
  FullyConstrained = true
  Placement = pos=(0,-14.3,2.37) rot=(-1,0,0;2.03453rad)
  sketch-geometry (4):
    g0: LineSegment StartX=0 StartY=1.5 StartZ=0 EndX=0 EndY=0 EndZ=0
    g1: LineSegment StartX=0 StartY=1.5 StartZ=0 EndX=5 EndY=1.5 EndZ=0
    g2: LineSegment StartX=5 StartY=1.5 StartZ=0 EndX=5 EndY=0 EndZ=0
    g3: LineSegment StartX=0 StartY=0 StartZ=0 EndX=5 EndY=0 EndZ=0
  constraints (13):
    c: Vertical(g0)
    c: Distance(g0) = 1.5
    c: Horizontal(g1)
    c: Distance(g1) = 5
    c: Coincident(g1,g0)
    c: Vertical(g2)
    c: Distance(g2) = 1.5
    c: Coincident(g2,g1)
    c: Block(g1)
    c: Block(g2)
    c: Block(g0)
    c: Coincident(g3,g0)
    c: Coincident(g3,g2)
FEATURE [Part::Extrusion] Extrude022  label="solenoidDriverBottomLipTopExtrude014"
  Base = -> Sketch025
  Dir = (0,0.894389,-0.447291)
  DirMode = 2
  FaceMakerClass = Part::FaceMakerBullseye
  LengthFwd = -6.5
  LengthRev = 0
  Placement = pos=(0,-15.45,20.3) rot=(1,0,0;1.5708rad)
  Solid = true
  Symmetric = false
FEATURE [Part::Fillet] Fillet013  label="solenoidDriverBottomLipTopFillet006"
  Base = -> Extrude022
  Edges = 1 edges r=1.4: [Edge6]
  Placement = pos=(5,0,0) rot=(0,0,1;0rad)
FEATURE [Sketcher::SketchObject] Sketch026
  FullyConstrained = true
  Placement = pos=(0,-14.3,2.37) rot=(-1,0,0;2.03453rad)
  sketch-geometry (4):
    g0: LineSegment StartX=0 StartY=1.5 StartZ=0 EndX=0 EndY=0 EndZ=0
    g1: LineSegment StartX=0 StartY=1.5 StartZ=0 EndX=5 EndY=1.5 EndZ=0
    g2: LineSegment StartX=5 StartY=1.5 StartZ=0 EndX=5 EndY=0 EndZ=0
    g3: LineSegment StartX=0 StartY=0 StartZ=0 EndX=5 EndY=0 EndZ=0
  constraints (13):
    c: Vertical(g0)
    c: Distance(g0) = 1.5
    c: Horizontal(g1)
    c: Distance(g1) = 5
    c: Coincident(g1,g0)
    c: Vertical(g2)
    c: Distance(g2) = 1.5
    c: Coincident(g2,g1)
    c: Block(g1)
    c: Block(g2)
    c: Block(g0)
    c: Coincident(g3,g0)
    c: Coincident(g3,g2)
FEATURE [Part::Extrusion] Extrude023  label="solenoidDriverBottomLipTopExtrude015"
  Base = -> Sketch026
  Dir = (0,0.894389,-0.447291)
  DirMode = 2
  FaceMakerClass = Part::FaceMakerBullseye
  LengthFwd = -6.5
  LengthRev = 0
  Placement = pos=(5,-14.15,19.65) rot=(1,0,0;1.5708rad)
  Solid = true
  Symmetric = false
FEATURE [Sketcher::SketchObject] Sketch027
  FullyConstrained = true
  Placement = pos=(0,-14.3,2.37) rot=(-1,0,0;2.03453rad)
  sketch-geometry (5):
    g0: LineSegment StartX=45.5 StartY=-21.2 StartZ=0 EndX=49.5 EndY=-21.2 EndZ=0
    g1: LineSegment StartX=49.5 StartY=0 StartZ=0 EndX=49.5 EndY=-21.2 EndZ=0
    g2: LineSegment StartX=49.5 StartY=0 StartZ=0 EndX=49.5 EndY=1.6 EndZ=0
    g3: LineSegment StartX=45.5 StartY=-21.2 StartZ=0 EndX=45.5 EndY=1.6 EndZ=0
    g4: LineSegment StartX=49.5 StartY=1.6 StartZ=0 EndX=45.5 EndY=1.6 EndZ=0
  constraints (14):
    c: Horizontal(g0)
    c: Distance(g0) = 4
    c: Coincident(g1,g0)
    c: Vertical(g1)
    c: Block(g1)
    c: Vertical(g2)
    c: Distance(g2) = 1.6
    c: Block(g2)
    c: Coincident(g3,g0)
    c: Vertical(g3)
    c: Coincident(g4,g2)
    c: Horizontal(g4)
    c: Block(g0)
    c: Coincident(g3,g4)
FEATURE [Part::Extrusion] Extrude024
  Base = -> Sketch027
  Dir = (0,0.894389,-0.447291)
  DirMode = 2
  FaceMakerClass = Part::FaceMakerBullseye
  LengthFwd = 6.34
  LengthRev = 0
  Placement = pos=(0,-5.59,1) rot=(0,0,1;0rad)
  Solid = true
  Symmetric = false
FEATURE [Part::Fillet] Fillet014  label="solenoidDriverSideBarFillet014"
  Base = -> Extrude024
  Edges = 1 edges r=1.4: [Edge14]
  Placement = pos=(0,0.9,-0.45) rot=(0,0,1;0rad)
FEATURE [Part::Revolution] Revolve  label="mainScrewStandRevolve"
  Angle = 360
  Axis = (0,0,1)
  Base = (0,0,0)
  FaceMakerClass = Part::FaceMakerBullseye
  Placement = pos=(121.35,-15.3,0) rot=(0,0,1;0rad)
  Solid = true
  Source = -> Sketch004
  Symmetric = false
FEATURE [Part::Extrusion] Extrude021  label="solenoidDriverTopLipLowerExtrude011"
  Base = -> Sketch024
  Dir = (0,0.894389,-0.447291)
  DirMode = 2
  FaceMakerClass = Part::FaceMakerBullseye
  LengthFwd = 5.05
  LengthRev = 0
  Solid = true
  Symmetric = false
FEATURE [Part::Fillet] Fillet012  label="solenoidDriverTopLipLowerFillet004"
  Base = -> Extrude021
  Edges = 1 edges r=1.2: [Edge7]
  Placement = pos=(0,-0.9,-1.35) rot=(0,0,1;0rad)
FEATURE [Part::Fillet] Fillet003  label="solenoidDriverTopLipLowerFillet003"
  Base = -> Extrude010
  Edges = 1 edges r=1.2: [Edge7]
  Placement = pos=(0,-3,-0.3) rot=(0,0,1;0rad)
FEATURE [Part::Extrusion] Extrude025  label="mainBodyUpperExtrude025"
  Base = -> Sketch001
  Dir = (0,0,1)
  DirMode = 2
  FaceMakerClass = Part::FaceMakerBullseye
  LengthFwd = 20
  LengthRev = 0
  Solid = true
  Symmetric = false
FEATURE [Part::MultiFuse] Fusion  label="solenoidDriverBottomLipFusion"
  Placement = pos=(0,-1.6,0) rot=(0,0,1;0rad)
  Shapes = -> [Fillet005,Fillet013,Extrude023,Extrude013]
FEATURE [Sketcher::SketchObject] Sketch028
  FullyConstrained = true
  Placement = pos=(0,-14.3,2.37) rot=(-1,0,0;2.03453rad)
  sketch-geometry (4):
    g0: LineSegment StartX=0 StartY=1.5 StartZ=0 EndX=0 EndY=0 EndZ=0
    g1: LineSegment StartX=0 StartY=1.5 StartZ=0 EndX=5 EndY=1.5 EndZ=0
    g2: LineSegment StartX=5 StartY=1.5 StartZ=0 EndX=5 EndY=0 EndZ=0
    g3: LineSegment StartX=0 StartY=0 StartZ=0 EndX=5 EndY=0 EndZ=0
  constraints (13):
    c: Vertical(g0)
    c: Distance(g0) = 1.5
    c: Horizontal(g1)
    c: Distance(g1) = 5
    c: Coincident(g1,g0)
    c: Vertical(g2)
    c: Distance(g2) = 1.5
    c: Coincident(g2,g1)
    c: Block(g1)
    c: Block(g2)
    c: Block(g0)
    c: Coincident(g3,g0)
    c: Coincident(g3,g2)
FEATURE [Part::Extrusion] Extrude026  label="solenoidDriverBottomLipTopExtrude016"
  Base = -> Sketch028
  Dir = (0,0.894389,-0.447291)
  DirMode = 2
  FaceMakerClass = Part::FaceMakerBullseye
  LengthFwd = -6.5
  LengthRev = 0
  Placement = pos=(5,-14.15,19.65) rot=(1,0,0;1.5708rad)
  Solid = true
  Symmetric = false
FEATURE [Sketcher::SketchObject] Sketch029
  FullyConstrained = true
  Placement = pos=(0,-14.3,2.37) rot=(-1,0,0;2.03453rad)
  sketch-geometry (4):
    g0: LineSegment StartX=0 StartY=1.5 StartZ=0 EndX=0 EndY=0 EndZ=0
    g1: LineSegment StartX=0 StartY=1.5 StartZ=0 EndX=5 EndY=1.5 EndZ=0
    g2: LineSegment StartX=5 StartY=1.5 StartZ=0 EndX=5 EndY=0 EndZ=0
    g3: LineSegment StartX=0 StartY=0 StartZ=0 EndX=5 EndY=0 EndZ=0
  constraints (13):
    c: Vertical(g0)
    c: Distance(g0) = 1.5
    c: Horizontal(g1)
    c: Distance(g1) = 5
    c: Coincident(g1,g0)
    c: Vertical(g2)
    c: Distance(g2) = 1.5
    c: Coincident(g2,g1)
    c: Block(g1)
    c: Block(g2)
    c: Block(g0)
    c: Coincident(g3,g0)
    c: Coincident(g3,g2)
FEATURE [Part::Extrusion] Extrude027  label="solenoidDriverBottomLipTopExtrude017"
  Base = -> Sketch029
  Dir = (0,0.894389,-0.447291)
  DirMode = 2
  FaceMakerClass = Part::FaceMakerBullseye
  LengthFwd = -6.5
  LengthRev = 0
  Placement = pos=(0,-14.15,19.65) rot=(1,0,0;1.5708rad)
  Solid = true
  Symmetric = false
FEATURE [Sketcher::SketchObject] Sketch030
  FullyConstrained = true
  Placement = pos=(0,-14.3,2.37) rot=(-1,0,0;2.03453rad)
  sketch-geometry (4):
    g0: LineSegment StartX=0 StartY=1.5 StartZ=0 EndX=0 EndY=0 EndZ=0
    g1: LineSegment StartX=0 StartY=1.5 StartZ=0 EndX=5 EndY=1.5 EndZ=0
    g2: LineSegment StartX=5 StartY=1.5 StartZ=0 EndX=5 EndY=0 EndZ=0
    g3: LineSegment StartX=0 StartY=0 StartZ=0 EndX=5 EndY=0 EndZ=0
  constraints (13):
    c: Vertical(g0)
    c: Distance(g0) = 1.5
    c: Horizontal(g1)
    c: Distance(g1) = 5
    c: Coincident(g1,g0)
    c: Vertical(g2)
    c: Distance(g2) = 1.5
    c: Coincident(g2,g1)
    c: Block(g1)
    c: Block(g2)
    c: Block(g0)
    c: Coincident(g3,g0)
    c: Coincident(g3,g2)
FEATURE [Sketcher::SketchObject] Sketch031
  FullyConstrained = true
  Placement = pos=(0,-14.3,2.37) rot=(-1,0,0;2.03453rad)
  sketch-geometry (6):
    g0: LineSegment StartX=45.5 StartY=-21.2 StartZ=0 EndX=49.5 EndY=-21.2 EndZ=0
    g1: LineSegment StartX=45.5 StartY=0 StartZ=0 EndX=49.5 EndY=0 EndZ=0
    g2: LineSegment StartX=49.5 StartY=0 StartZ=0 EndX=49.5 EndY=-21.2 EndZ=0
    g3: LineSegment StartX=4 StartY=0 StartZ=0 EndX=4 EndY=-21.2 EndZ=0
    g4: LineSegment StartX=45.5 StartY=-21.2 StartZ=0 EndX=4 EndY=-21.2 EndZ=0
    g5: LineSegment StartX=4 StartY=0 StartZ=0 EndX=45.5 EndY=0 EndZ=0
  constraints (16):
    c: Horizontal(g0)
    c: Distance(g0) = 4
    c: Horizontal(g1)
    c: Distance(g1) = 4
    c: Coincident(g2,g1)
    c: Coincident(g2,g0)
    c: Vertical(g2)
    c: Block(g2)
    c: Vertical(g3)
    c: Coincident(g4,g0)
    c: Horizontal(g4)
    c: Coincident(g4,g3)
    c: Coincident(g5,g1)
    c: Horizontal(g5)
    c: Block(g3)
    c: Block(g5)
FEATURE [Part::Extrusion] Extrude028  label="removeFromSolenoidDriverMainExtrude021"
  Base = -> Sketch031
  Dir = (0,0.894389,-0.447291)
  DirMode = 2
  FaceMakerClass = Part::FaceMakerBullseye
  LengthFwd = 3.1
  LengthRev = 0
  Placement = pos=(-4,-2.42,-0.8) rot=(0,0,1;0rad)
  Solid = true
  Symmetric = false
FEATURE [Part::Extrusion] Extrude029  label="solenoidDriverBottomLipTopExtrude018"
  Base = -> Sketch030
  Dir = (0,0.894389,-0.447291)
  DirMode = 2
  FaceMakerClass = Part::FaceMakerBullseye
  LengthFwd = -6.5
  LengthRev = 0
  Placement = pos=(5,-14.15,19.65) rot=(1,0,0;1.5708rad)
  Solid = true
  Symmetric = false
FEATURE [Sketcher::SketchObject] Sketch032
  FullyConstrained = true
  Placement = pos=(0,-14.3,2.37) rot=(-1,0,0;2.03453rad)
  sketch-geometry (4):
    g0: LineSegment StartX=0 StartY=1.5 StartZ=0 EndX=0 EndY=0 EndZ=0
    g1: LineSegment StartX=0 StartY=1.5 StartZ=0 EndX=5 EndY=1.5 EndZ=0
    g2: LineSegment StartX=5 StartY=1.5 StartZ=0 EndX=5 EndY=0 EndZ=0
    g3: LineSegment StartX=0 StartY=0 StartZ=0 EndX=5 EndY=0 EndZ=0
  constraints (13):
    c: Vertical(g0)
    c: Distance(g0) = 1.5
    c: Horizontal(g1)
    c: Distance(g1) = 5
    c: Coincident(g1,g0)
    c: Vertical(g2)
    c: Distance(g2) = 1.5
    c: Coincident(g2,g1)
    c: Block(g1)
    c: Block(g2)
    c: Block(g0)
    c: Coincident(g3,g0)
    c: Coincident(g3,g2)
FEATURE [Part::Extrusion] Extrude030  label="solenoidDriverBottomLipTopExtrude019"
  Base = -> Sketch032
  Dir = (0,0.894389,-0.447291)
  DirMode = 2
  FaceMakerClass = Part::FaceMakerBullseye
  LengthFwd = -6.5
  LengthRev = 0
  Placement = pos=(0,-14.15,19.65) rot=(1,0,0;1.5708rad)
  Solid = true
  Symmetric = false
FEATURE [Part::MultiFuse] Fusion004
  Placement = pos=(0,1.4,2.65) rot=(0,0,1;0rad)
  Shapes = -> [Extrude029,Extrude030]
FEATURE [Part::MultiFuse] Fusion003
  Placement = pos=(-2.3,0,0) rot=(0,0,1;0rad)
  Shapes = -> [Extrude028,Fusion004]
FEATURE [Sketcher::SketchObject] Sketch033
  FullyConstrained = true
  Placement = pos=(0,-14.3,2.37) rot=(-1,0,0;2.03453rad)
  sketch-geometry (4):
    g0: LineSegment StartX=0 StartY=1.5 StartZ=0 EndX=0 EndY=0 EndZ=0
    g1: LineSegment StartX=0 StartY=1.5 StartZ=0 EndX=5 EndY=1.5 EndZ=0
    g2: LineSegment StartX=5 StartY=1.5 StartZ=0 EndX=5 EndY=0 EndZ=0
    g3: LineSegment StartX=0 StartY=0 StartZ=0 EndX=5 EndY=0 EndZ=0
  constraints (13):
    c: Vertical(g0)
    c: Distance(g0) = 1.5
    c: Horizontal(g1)
    c: Distance(g1) = 5
    c: Coincident(g1,g0)
    c: Vertical(g2)
    c: Distance(g2) = 1.5
    c: Coincident(g2,g1)
    c: Block(g1)
    c: Block(g2)
    c: Block(g0)
    c: Coincident(g3,g0)
    c: Coincident(g3,g2)
FEATURE [Sketcher::SketchObject] Sketch034
  FullyConstrained = true
  Placement = pos=(0,-14.3,2.37) rot=(-1,0,0;2.03453rad)
  sketch-geometry (4):
    g0: LineSegment StartX=0 StartY=1.5 StartZ=0 EndX=0 EndY=0 EndZ=0
    g1: LineSegment StartX=0 StartY=1.5 StartZ=0 EndX=5 EndY=1.5 EndZ=0
    g2: LineSegment StartX=5 StartY=1.5 StartZ=0 EndX=5 EndY=0 EndZ=0
    g3: LineSegment StartX=0 StartY=0 StartZ=0 EndX=5 EndY=0 EndZ=0
  constraints (13):
    c: Vertical(g0)
    c: Distance(g0) = 1.5
    c: Horizontal(g1)
    c: Distance(g1) = 5
    c: Coincident(g1,g0)
    c: Vertical(g2)
    c: Distance(g2) = 1.5
    c: Coincident(g2,g1)
    c: Block(g1)
    c: Block(g2)
    c: Block(g0)
    c: Coincident(g3,g0)
    c: Coincident(g3,g2)
FEATURE [Part::Extrusion] Extrude020  label="removeFromSolenoidDriverMainExtrude020"
  Base = -> Sketch020
  Dir = (0,0.894389,-0.447291)
  DirMode = 2
  FaceMakerClass = Part::FaceMakerBullseye
  LengthFwd = 3.1
  LengthRev = 0
  Placement = pos=(-4,-2.42,-0.8) rot=(0,0,1;0rad)
  Solid = true
  Symmetric = false
FEATURE [Part::Fillet] Fillet
  Base = -> Fusion003
  Edges = 1 edges r=10: [Edge5]
  Placement = pos=(-2,0,0) rot=(0,0,1;0rad)
FEATURE [Part::MultiFuse] Fusion001
  Placement = pos=(0,1.4,2.65) rot=(0,0,1;0rad)
  Shapes = -> [Extrude026,Extrude027]
FEATURE [Part::MultiFuse] Fusion002
  Shapes = -> [Extrude020,Fusion001]
FEATURE [Sketcher::SketchObject] Sketch035
  FullyConstrained = true
  Placement = pos=(0,-14.3,2.37) rot=(-1,0,0;2.03453rad)
  sketch-geometry (4):
    g0: LineSegment StartX=0 StartY=1.5 StartZ=0 EndX=0 EndY=0 EndZ=0
    g1: LineSegment StartX=0 StartY=1.5 StartZ=0 EndX=5 EndY=1.5 EndZ=0
    g2: LineSegment StartX=5 StartY=1.5 StartZ=0 EndX=5 EndY=0 EndZ=0
    g3: LineSegment StartX=0 StartY=0 StartZ=0 EndX=5 EndY=0 EndZ=0
  constraints (13):
    c: Vertical(g0)
    c: Distance(g0) = 1.5
    c: Horizontal(g1)
    c: Distance(g1) = 5
    c: Coincident(g1,g0)
    c: Vertical(g2)
    c: Distance(g2) = 1.5
    c: Coincident(g2,g1)
    c: Block(g1)
    c: Block(g2)
    c: Block(g0)
    c: Coincident(g3,g0)
    c: Coincident(g3,g2)
FEATURE [Sketcher::SketchObject] Sketch036
  FullyConstrained = true
  Placement = pos=(0,-14.3,2.37) rot=(-1,0,0;2.03453rad)
  sketch-geometry (4):
    g0: LineSegment StartX=0 StartY=1.5 StartZ=0 EndX=0 EndY=0 EndZ=0
    g1: LineSegment StartX=0 StartY=1.5 StartZ=0 EndX=5 EndY=1.5 EndZ=0
    g2: LineSegment StartX=5 StartY=1.5 StartZ=0 EndX=5 EndY=0 EndZ=0
    g3: LineSegment StartX=0 StartY=0 StartZ=0 EndX=5 EndY=0 EndZ=0
  constraints (13):
    c: Vertical(g0)
    c: Distance(g0) = 1.5
    c: Horizontal(g1)
    c: Distance(g1) = 5
    c: Coincident(g1,g0)
    c: Vertical(g2)
    c: Distance(g2) = 1.5
    c: Coincident(g2,g1)
    c: Block(g1)
    c: Block(g2)
    c: Block(g0)
    c: Coincident(g3,g0)
    c: Coincident(g3,g2)
FEATURE [Part::Extrusion] Extrude031  label="solenoidDriverBottomLipTopExtrude020"
  Base = -> Sketch035
  Dir = (0,0.894389,-0.447291)
  DirMode = 2
  FaceMakerClass = Part::FaceMakerBullseye
  LengthFwd = -6.5
  LengthRev = 0
  Placement = pos=(5,-14.15,19.65) rot=(1,0,0;1.5708rad)
  Solid = true
  Symmetric = false
FEATURE [Part::Extrusion] Extrude032  label="solenoidDriverBottomLipTopExtrude021"
  Base = -> Sketch036
  Dir = (0,0.894389,-0.447291)
  DirMode = 2
  FaceMakerClass = Part::FaceMakerBullseye
  LengthFwd = -6.5
  LengthRev = 0
  Placement = pos=(0,-14.15,19.65) rot=(1,0,0;1.5708rad)
  Solid = true
  Symmetric = false
FEATURE [Part::MultiFuse] Fusion009
  Placement = pos=(8,1.4,2.65) rot=(0,0,1;0rad)
  Shapes = -> [Extrude031,Extrude032]
FEATURE [Part::MultiFuse] Fusion010  label="removeFromSolenoidDriver"
  Shapes = -> [Fusion009,Fillet,Fusion002]
FEATURE [Sketcher::SketchObject] Sketch037
  FullyConstrained = true
  Placement = pos=(0,0,0) rot=(1,0,0;1.5708rad)
  sketch-geometry (4):
    g0: Circle CenterX=64.05 CenterY=16.5 CenterZ=0 NormalX=0 NormalY=0 NormalZ=1 AngleXU=0 Radius=2.7
    g1: Circle CenterX=64.05 CenterY=8.5 CenterZ=0 NormalX=0 NormalY=0 NormalZ=1 AngleXU=0 Radius=2.7
    g2: Circle CenterX=84.15 CenterY=8.5 CenterZ=0 NormalX=0 NormalY=0 NormalZ=1 AngleXU=0 Radius=2.7
    g3: Circle CenterX=84.15 CenterY=16.5 CenterZ=0 NormalX=0 NormalY=0 NormalZ=1 AngleXU=0 Radius=2.7
  constraints (4):
    c: Block(g2)
    c: Block(g3)
    c: Block(g0)
    c: Block(g1)
FEATURE [Part::Extrusion] Extrude033  label="removeFromMainBodyToCreateScrewHoleCounterSinks001"
  Base = -> Sketch037
  Dir = (0,-1,1.1e-15)
  DirMode = 2
  FaceMakerClass = Part::FaceMakerBullseye
  LengthFwd = 1.9
  LengthRev = 0
  Placement = pos=(0.8,0,0) rot=(0,0,1;0rad)
  Solid = true
  Symmetric = false
FEATURE [Part::MultiFuse] Fusion011  label="removeFromMainBodyToCreateScrewHoleCounterSinks001Fusion011"
  Shapes = -> [Extrude014,Extrude033]
FEATURE [Sketcher::SketchObject] Sketch038
  FullyConstrained = true
  Placement = pos=(0,-14.3,2.37) rot=(-1,0,0;2.03453rad)
  sketch-geometry (4):
    g0: LineSegment StartX=33.9 StartY=-9.7 StartZ=0 EndX=33.9 EndY=-1.5 EndZ=0
    g1: LineSegment StartX=33.9 StartY=-1.5 StartZ=0 EndX=44.5 EndY=-1.5 EndZ=0
    g2: LineSegment StartX=33.9 StartY=-9.7 StartZ=0 EndX=44.5 EndY=-9.7 EndZ=0
    g3: LineSegment StartX=44.5 StartY=-1.5 StartZ=0 EndX=44.5 EndY=-9.7 EndZ=0
  constraints (10):
    c: Vertical(g0)
    c: Coincident(g1,g0)
    c: Horizontal(g1)
    c: Block(g1)
    c: Block(g0)
    c: Coincident(g2,g0)
    c: Horizontal(g2)
    c: Coincident(g3,g1)
    c: Coincident(g3,g2)
    c: Vertical(g3)
FEATURE [Part::Extrusion] Extrude034
  Base = -> Sketch038
  Dir = (0,0.894389,-0.447291)
  DirMode = 2
  FaceMakerClass = Part::FaceMakerBullseye
  LengthFwd = 16
  LengthRev = 0
  Placement = pos=(0,-22,7) rot=(0,0,1;0rad)
  Solid = true
  Symmetric = false
FEATURE [Sketcher::SketchObject] Sketch039
  FullyConstrained = true
  Placement = pos=(0,-14.3,2.37) rot=(-1,0,0;2.03453rad)
  sketch-geometry (4):
    g0: LineSegment StartX=5.5 StartY=-7.7 StartZ=0 EndX=13.3 EndY=-7.7 EndZ=0
    g1: LineSegment StartX=13.3 StartY=-7.7 StartZ=0 EndX=13.3 EndY=-13.1 EndZ=0
    g2: LineSegment StartX=13.3 StartY=-13.1 StartZ=0 EndX=5.5 EndY=-13.1 EndZ=0
    g3: LineSegment StartX=5.5 StartY=-7.7 StartZ=0 EndX=5.5 EndY=-13.1 EndZ=0
  constraints (12):
    c: Horizontal(g0)
    c: Distance(g0) = 7.8
    c: Coincident(g1,g0)
    c: Vertical(g1)
    c: Distance(g1) = 5.4
    c: Coincident(g2,g1)
    c: Horizontal(g2)
    c: Vertical(g3)
    c: Coincident(g3,g2)
    c: Block(g0)
    c: Block(g2)
    c: Block(g3)
FEATURE [Part::Extrusion] Extrude035  label="removeToMakeHoleForConnectorExtrude035"
  Base = -> Sketch039
  Dir = (0,0.894389,-0.447291)
  DirMode = 2
  FaceMakerClass = Part::FaceMakerBullseye
  LengthFwd = 15
  LengthRev = 0
  Placement = pos=(-4,-22,9.6469) rot=(0,0,1;0rad)
  Solid = true
  Symmetric = false
FEATURE [App::MeasureDistance] Distance  label="Distance: 4.00 mm"
  Distance = 4.00184
  P1 = (119.349,-15.3,8)
  P2 = (123.351,-15.3,8)
FEATURE [App::MeasureDistance] Distance001  label="Distance: 3.80 mm"
  Distance = 3.8
  P1 = (119.45,-15.3,8)
  P2 = (123.25,-15.3,8)
FEATURE [Part::Fillet] Fillet015
  Base = -> Extrude009
  Edges = 1 edges r=1.59: [Edge7]
FEATURE [Part::Fillet] Fillet016
  Base = -> Extrude017
  Edges = 1 edges r=1.49: [Edge12]
FEATURE [Part::Fillet] Fillet017
  Base = -> Fillet016
  Edges = 1 edges r=1.45: [Edge8]
FEATURE [Part::MultiFuse] Fusion012  label="main"
  Shapes = -> [Extrude,Revolve,Extrude005,Fillet003,Fillet012,Fillet014,Extrude025,Fusion,Fillet015,Fillet017]
FEATURE [Part::Cut] Cut001
  Base = -> Fusion012
  Tool = -> Box003
FEATURE [Part::Cut] Cut002
  Base = -> Cut001
  Tool = -> Box002
FEATURE [Part::Cut] Cut003
  Base = -> Cut002
  Tool = -> Cut
FEATURE [Part::Cut] Cut004
  Base = -> Cut003
  Tool = -> Extrude019
FEATURE [Part::Cut] Cut005
  Base = -> Cut004
  Tool = -> Fusion011
FEATURE [Part::Cut] Cut006
  Base = -> Cut005
  Tool = -> Extrude004
FEATURE [Part::Cut] Cut007
  Base = -> Cut006
  Tool = -> Extrude015
FEATURE [Part::Cut] Cut008
  Base = -> Cut007
  Tool = -> Extrude008
FEATURE [Part::Cut] Cut009
  Base = -> Cut008
  Tool = -> Fusion010
FEATURE [App::MeasureDistance] Distance002  label="Distance: 2.05 mm"
  Distance = 2.05453
  P1 = (1.5,-23.0732,21.402)
  P2 = (6e-15,-23,20)
FEATURE [Part::Cut] Cut010
  Base = -> Cut009
  Tool = -> Extrude035
FEATURE [Part::Cut] Cut011
  Base = -> Cut010
  Tool = -> Extrude034
FEATURE [Part::Fillet] Fillet018
  Base = -> Cut011
  Edges = 1 edges r=3: [Edge134]
FEATURE [Part::Fillet] Fillet019
  Base = -> Fillet018
  Edges = 1 edges r=3: [Edge29]
FEATURE [Part::Box] Box004  label="Cube004"
  AttacherType = Attacher::AttachEngine3D
  Height = 10
  Length = 200
  Placement = pos=(-30,0,0) rot=(0,0,1;0rad)
  Width = 10
FEATURE [Part::Fillet] Fillet020
  Base = -> Box004
  Edges = 1 edges r=3.6: [Edge12]
FEATURE [Part::Box] Box005  label="Cube005"
  AttacherType = Attacher::AttachEngine3D
  Height = 10
  Length = 198
  Placement = pos=(-30,0,0) rot=(0,0,1;0rad)
  Width = 10
FEATURE [Part::Cut] Cut012
  Base = -> Box005
  Tool = -> Fillet020
FEATURE [Part::Box] Box006  label="Cube006"
  AttacherType = Attacher::AttachEngine3D
  Height = 5
  Length = 200
  Placement = pos=(-30,6.4,10) rot=(1,0,0;0rad)
  Width = 5
FEATURE [Part::Box] Box007  label="Cube007"
  AttacherType = Attacher::AttachEngine3D
  Height = 5
  Length = 200
  Placement = pos=(-30,6.4,10) rot=(1,0,0;0.872665rad)
  Width = 5
FEATURE [Part::MultiFuse] Fusion013  label="removeFromMainFusion013"
  Placement = pos=(0,-10,10) rot=(0,0,1;0rad)
  Shapes = -> [Box007,Box006,Cut012]
FEATURE [Part::Cut] Cut013
  Base = -> Fillet019
  Tool = -> Fusion013
FEATURE [Mesh::Feature] v0_98_Cut013  label="v0_98-Cut013"
FEATURE [App::MeasureDistance] Distance003  label="Distance: 7.18 mm"
  Distance = 7.17719
  P1 = (117.773,-15.3145,-2.4)
  P2 = (124.951,-15.2973,-2.4)
FEATURE [Sketcher::SketchObject] Sketch040
  FullyConstrained = true
  Placement = pos=(0,-14.3,2.37) rot=(-1,0,0;2.03453rad)
  sketch-geometry (4):
    g0: LineSegment StartX=0 StartY=1.5 StartZ=0 EndX=0 EndY=0 EndZ=0
    g1: LineSegment StartX=0 StartY=1.5 StartZ=0 EndX=5 EndY=1.5 EndZ=0
    g2: LineSegment StartX=5 StartY=1.5 StartZ=0 EndX=5 EndY=0 EndZ=0
    g3: LineSegment StartX=0 StartY=0 StartZ=0 EndX=5 EndY=0 EndZ=0
  constraints (13):
    c: Vertical(g0)
    c: Distance(g0) = 1.5
    c: Horizontal(g1)
    c: Distance(g1) = 5
    c: Coincident(g1,g0)
    c: Vertical(g2)
    c: Distance(g2) = 1.5
    c: Coincident(g2,g1)
    c: Block(g1)
    c: Block(g2)
    c: Block(g0)
    c: Coincident(g3,g0)
    c: Coincident(g3,g2)
FEATURE [Part::Extrusion] Extrude036
  Base = -> Sketch040
  Dir = (0,0.894389,-0.447291)
  DirMode = 2
  FaceMakerClass = Part::FaceMakerBullseye
  LengthFwd = 1.4
  LengthRev = 0
  Placement = pos=(0,8.25,17.58) rot=(0,0,1;0rad)
  Solid = true
  Symmetric = false
FEATURE [Sketcher::SketchObject] Sketch041
  FullyConstrained = true
  Placement = pos=(0,-14.3,2.37) rot=(-1,0,0;2.03453rad)
  sketch-geometry (4):
    g0: LineSegment StartX=0 StartY=1.5 StartZ=0 EndX=0 EndY=0 EndZ=0
    g1: LineSegment StartX=0 StartY=1.5 StartZ=0 EndX=5 EndY=1.5 EndZ=0
    g2: LineSegment StartX=5 StartY=1.5 StartZ=0 EndX=5 EndY=0 EndZ=0
    g3: LineSegment StartX=0 StartY=0 StartZ=0 EndX=5 EndY=0 EndZ=0
  constraints (13):
    c: Vertical(g0)
    c: Distance(g0) = 1.5
    c: Horizontal(g1)
    c: Distance(g1) = 5
    c: Coincident(g1,g0)
    c: Vertical(g2)
    c: Distance(g2) = 1.5
    c: Coincident(g2,g1)
    c: Block(g1)
    c: Block(g2)
    c: Block(g0)
    c: Coincident(g3,g0)
    c: Coincident(g3,g2)
FEATURE [Part::Extrusion] Extrude037
  Base = -> Sketch041
  Dir = (0,0.894389,-0.447291)
  DirMode = 2
  FaceMakerClass = Part::FaceMakerBullseye
  LengthFwd = 1.4
  LengthRev = 0
  Placement = pos=(0,6.11,13.33) rot=(0,0,1;0rad)
  Solid = true
  Symmetric = false
FEATURE [Part::MultiFuse] Fusion014  label="screwSpacerFusion014"
  Shapes = -> [Extrude037,Extrude036]
FEATURE [Sketcher::SketchObject] Sketch042
  FullyConstrained = true
  Placement = pos=(0,-14.3,2.37) rot=(-1,0,0;2.03453rad)
  sketch-geometry (4):
    g0: LineSegment StartX=0 StartY=1.5 StartZ=0 EndX=0 EndY=0 EndZ=0
    g1: LineSegment StartX=0 StartY=1.5 StartZ=0 EndX=5 EndY=1.5 EndZ=0
    g2: LineSegment StartX=5 StartY=1.5 StartZ=0 EndX=5 EndY=0 EndZ=0
    g3: LineSegment StartX=0 StartY=0 StartZ=0 EndX=5 EndY=0 EndZ=0
  constraints (13):
    c: Vertical(g0)
    c: Distance(g0) = 1.5
    c: Horizontal(g1)
    c: Distance(g1) = 5
    c: Coincident(g1,g0)
    c: Vertical(g2)
    c: Distance(g2) = 1.5
    c: Coincident(g2,g1)
    c: Block(g1)
    c: Block(g2)
    c: Block(g0)
    c: Coincident(g3,g0)
    c: Coincident(g3,g2)
FEATURE [Part::Extrusion] Extrude038
  Base = -> Sketch042
  Dir = (0,0.894389,-0.447291)
  DirMode = 2
  FaceMakerClass = Part::FaceMakerBullseye
  LengthFwd = 1.4
  LengthRev = 0
  Placement = pos=(0,8.459,18) rot=(0,0,1;0rad)
  Solid = true
  Symmetric = false
FEATURE [Part::MultiFuse] Fusion015  label="screwSpacerFusion014Fusion015"
  Placement = pos=(0,0.35,-0.18) rot=(0,0,1;0rad)
  Shapes = -> [Extrude038,Fusion014]
FEATURE [Part::Cylinder] Cylinder
  Angle = 360
  AttacherType = Attacher::AttachEngine3D
  Height = 10
  Placement = pos=(0,10,0) rot=(0,0,1;0rad)
  Radius = 1.5
FEATURE [Part::Cylinder] Cylinder001
  Angle = 360
  AttacherType = Attacher::AttachEngine3D
  Height = 10
  Placement = pos=(3,10,0) rot=(0,0,1;0rad)
  Radius = 1.5
FEATURE [Part::Box] Box008  label="Cube008"
  AttacherType = Attacher::AttachEngine3D
  Height = 10
  Length = 3
  Placement = pos=(0,8.5,0) rot=(0,0,1;0rad)
  Width = 3
FEATURE [Part::MultiFuse] Fusion016  label="holeForWireFusion016"
  Shapes = -> [Cylinder001,Box008,Cylinder]
FEATURE [Part::Box] Box009  label="Cube009"
  AttacherType = Attacher::AttachEngine3D
  Height = 10
  Length = 3
  Placement = pos=(0,8.5,0) rot=(0,0,1;0rad)
  Width = 3
FEATURE [Part::Cylinder] Cylinder002
  Angle = 360
  AttacherType = Attacher::AttachEngine3D
  Height = 10
  Placement = pos=(0,10,0) rot=(0,0,1;0rad)
  Radius = 1.5
FEATURE [Part::Cylinder] Cylinder003
  Angle = 360
  AttacherType = Attacher::AttachEngine3D
  Height = 10
  Placement = pos=(3,10,0) rot=(0,0,1;0rad)
  Radius = 1.5
FEATURE [Part::MultiFuse] Fusion017  label="holeForWireFusion017"
  Placement = pos=(0,0,10) rot=(0,0,1;0rad)
  Shapes = -> [Cylinder003,Box009,Cylinder002]
FEATURE [Part::MultiFuse] Fusion018  label="holeForWireFusion018"
  Placement = pos=(0,0,0) rot=(0,1,0;-1.5708rad)
  Shapes = -> [Fusion017,Fusion016]
FEATURE [Part::Box] Box010  label="Cube010"
  AttacherType = Attacher::AttachEngine3D
  Height = 0.1
  Length = 0.1
  Placement = pos=(-2,10,0) rot=(0,0.995037,0.099504;0rad)
  Width = 0.1
FEATURE [Part::MultiFuse] Fusion019
  Placement = pos=(0,10,0) rot=(1,0,0;1.5708rad)
  Shapes = -> [Box010,Fusion018]
FEATURE [Part::Box] Box011  label="Cube011"
  AttacherType = Attacher::AttachEngine3D
  Height = 0.1
  Length = 1.1
  Placement = pos=(-2,10,10) rot=(0,0.995037,0.099504;0rad)
  Width = 0.1
FEATURE [Part::MultiFuse] Fusion020
  Placement = pos=(0,0,0) rot=(0,1,0;0.349066rad)
  Shapes = -> [Box011,Fusion019]
FEATURE [Part::Box] Box012  label="Cube012"
  AttacherType = Attacher::AttachEngine3D
  Height = 0.1
  Length = 1.1
  Placement = pos=(-2,10,10) rot=(0,0.995037,0.099504;0rad)
  Width = 0.1
FEATURE [Part::MultiFuse] Fusion021
  Placement = pos=(0,30,0) rot=(0,0,1;-2.6529rad)
  Shapes = -> [Box012,Fusion020]
FEATURE [Part::Box] Box013  label="Cube013"
  AttacherType = Attacher::AttachEngine3D
  Height = 0.1
  Length = 1.1
  Placement = pos=(2,19,10) rot=(0,0.995037,0.099504;0rad)
  Width = 0.1
FEATURE [Part::MultiFuse] Fusion022  label="holeForWire"
  Shapes = -> [Box013,Fusion021]
